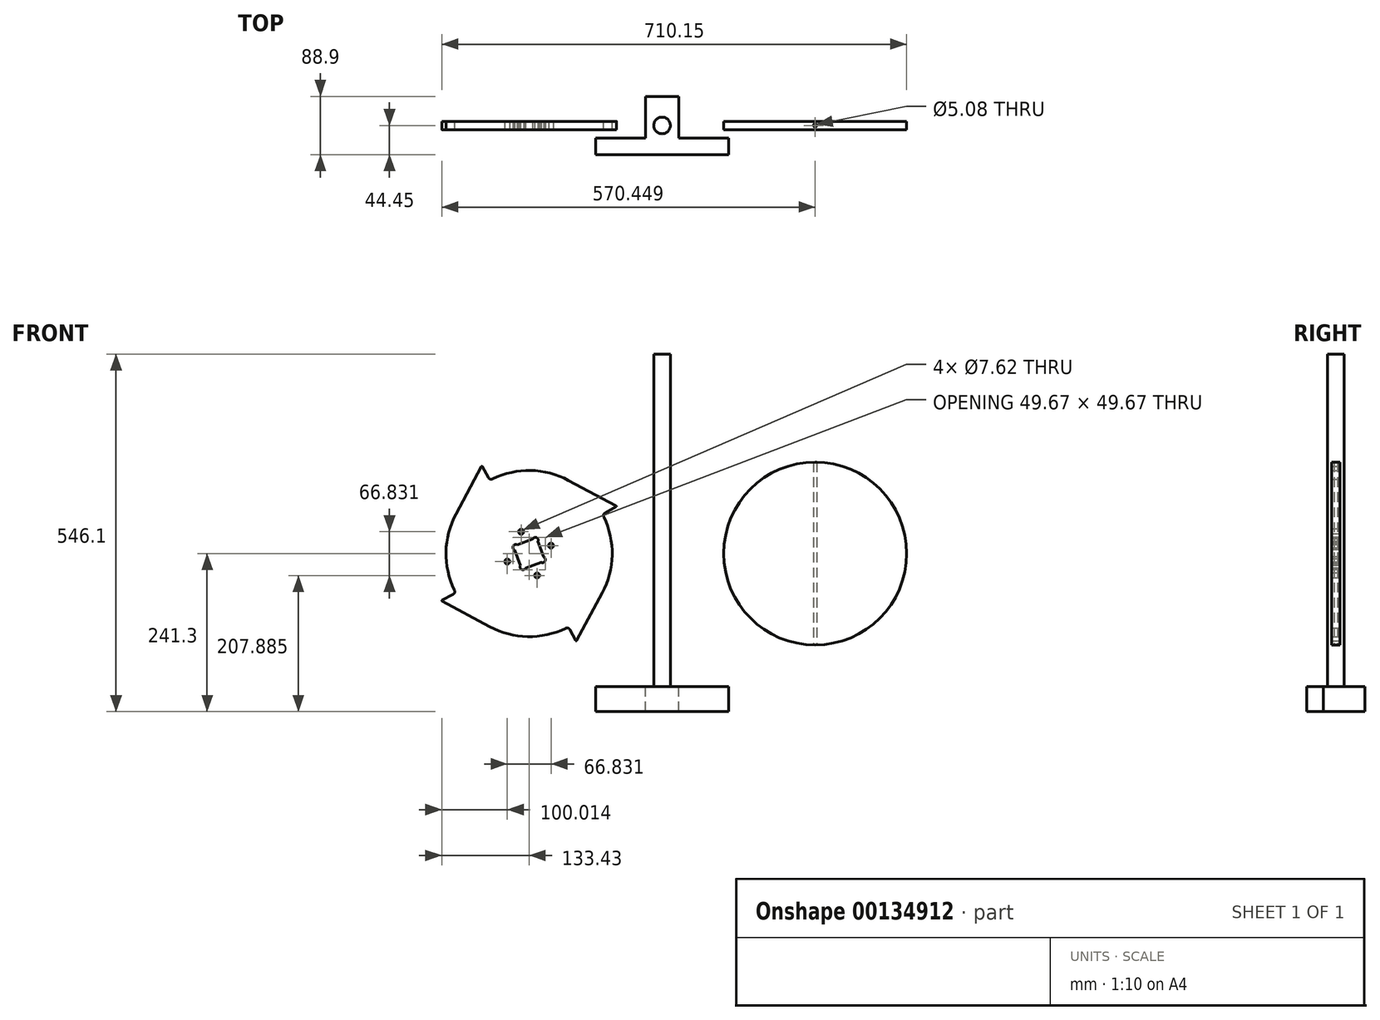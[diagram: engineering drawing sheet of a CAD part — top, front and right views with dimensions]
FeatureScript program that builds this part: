
annotation { "Feature Type Name" : "Feature", "Feature Type Description" : "" }
export const myFeature = defineFeature(function(context is Context, id is Id, definition is map)
    precondition{}
    {
        {
            var Q0;
            Q0=qCreatedBy(makeId("Front.planeOp"),FACE);
            var sketch = newSketch(context, id + "F0", { "sketchPlane" : qUnion([Q0])});
            skLineSegment(sketch, "E0", {"start": v(-203.2, 203.2) * mm, "end": v(-95.44, 310.96) * mm, "construction": true});
            skLineSegment(sketch, "E1", {"start": v(-203.2, 203.2) * mm, "end": v(-95.44, 95.44) * mm, "construction": true});
            skLineSegment(sketch, "E2", {"start": v(-203.2, 203.2) * mm, "end": v(-310.96, 95.44) * mm, "construction": true});
            skLineSegment(sketch, "E3", {"start": v(-203.2, 203.2) * mm, "end": v(-203.2, 409.98) * mm, "construction": true});
            skLineSegment(sketch, "E4", {"start": v(-91.3, 263.26) * mm, "end": v(-68.92, 275.27) * mm});
            skLineSegment(sketch, "E5", {"start": v(-143.14, 91.3) * mm, "end": v(-131.13, 68.92) * mm});
            skLineSegment(sketch, "E6", {"start": v(-315.1, 143.14) * mm, "end": v(-337.48, 131.13) * mm});
            skArc(sketch, "E7", {"start": v(-91.3, 263.26) * mm, "mid": v(-76.2, 203.2) * mm, "end": v(-91.3, 143.14) * mm});
            skArc(sketch, "E8", {"start": v(-143.14, 91.3) * mm, "mid": v(-203.2, 76.2) * mm, "end": v(-263.26, 91.3) * mm});
            skArc(sketch, "E9", {"start": v(-315.1, 143.14) * mm, "mid": v(-330.2, 203.2) * mm, "end": v(-315.1, 263.26) * mm});
            skLineSegment(sketch, "E10", {"start": v(-143.14, 315.1) * mm, "end": v(-68.92, 275.27) * mm});
            skLineSegment(sketch, "E11", {"start": v(-131.13, 68.92) * mm, "end": v(-91.3, 143.14) * mm});
            skLineSegment(sketch, "E12", {"start": v(-337.48, 131.13) * mm, "end": v(-263.26, 91.3) * mm});
            skLineSegment(sketch, "E13", {"start": v(-203.2, 203.2) * mm, "end": v(-293, 293) * mm, "construction": true});
            skArc(sketch, "E14.trimOffspring", {"start": v(-263.26, 315.1) * mm, "mid": v(-203.2, 330.2) * mm, "end": v(-143.14, 315.1) * mm});
            skLineSegment(sketch, "E15", {"start": v(-263.26, 315.1) * mm, "end": v(-275.27, 337.48) * mm});
            skLineSegment(sketch, "E16", {"start": v(-275.27, 337.48) * mm, "end": v(-315.1, 263.26) * mm});
            skSolve(sketch);
        }
        {
            var Q0;
            Q0=makeQuery(id+"F0.imprint","IMPRINT",FACE,{"disambiguationData":[TD([[makeQuery(id+"F0.imprint","IMPRINT",EDGE,{"derivedFrom":sQuery(id+"F0.wireOp",EDGE,"E4")}),1.0]])]});
            extrude(context, id + "F1", {"entities" : qUnion([Q0]), "endBound" : BoundingType.SYMMETRIC, "depth" : 12.7 * mm});
        }
        {
            var Q0;
            Q0=qCreatedBy(makeId("Front.planeOp"),FACE);
            var sketch = newSketch(context, id + "F2", { "sketchPlane" : qUnion([Q0])});
            skArc(sketch, "E17.0", {"start": v(-315.1, 143.14) * mm, "mid": v(-330.2, 203.2) * mm, "end": v(-315.1, 263.26) * mm, "construction": true});
            skLineSegment(sketch, "E18", {"start": v(-203.2, 203.2) * mm, "end": v(-57.25, 256.32) * mm, "construction": true});
            skLineSegment(sketch, "E19", {"start": v(-203.2, 203.2) * mm, "end": v(-203.2, 358.54) * mm, "construction": true});
            skLineSegment(sketch, "E20", {"start": v(-203.2, 203.2) * mm, "end": v(-359.68, 203.2) * mm, "construction": true});
            skPoint(sketch, "E20.endSnap0", {"position": v(-330.2, 203.2) * mm});
            skLineSegment(sketch, "E21", {"start": v(-203.2, 203.2) * mm, "end": v(-256.47, 349.55) * mm, "construction": true});
            skLineSegment(sketch, "E22", {"start": v(-227.62, 214.59) * mm, "end": v(-191.81, 227.62) * mm});
            skLineSegment(sketch, "E23", {"start": v(-191.81, 227.62) * mm, "end": v(-178.78, 191.81) * mm});
            skLineSegment(sketch, "E24", {"start": v(-178.78, 191.81) * mm, "end": v(-214.59, 178.78) * mm});
            skLineSegment(sketch, "E25", {"start": v(-227.62, 214.59) * mm, "end": v(-214.59, 178.78) * mm});
            skCircle(sketch, "E26", {"center": v(-169.78, 215.36) * mm, "radius": 3.81 * mm});
            skCircle(sketch, "E27", {"center": v(-215.36, 236.62) * mm, "radius": 3.81 * mm});
            skCircle(sketch, "E28.MirrorC", {"center": v(-236.62, 191.04) * mm, "radius": 3.81 * mm});
            skCircle(sketch, "E29.MirrorC", {"center": v(-191.04, 169.78) * mm, "radius": 3.81 * mm});
            skLineSegment(sketch, "E30", {"start": v(-203.2, 203.2) * mm, "end": v(-191.81, 227.62) * mm, "construction": true});
            skCircle(sketch, "E31", {"center": v(-193.71, 223.55) * mm, "radius": 4.5 * mm});
            skPoint(sketch, "E31.first.point", {"position": v(-189.64, 221.65) * mm});
            skPoint(sketch, "E31.second.point", {"position": v(-197.78, 225.44) * mm});
            skCircle(sketch, "E32.MirrorC", {"center": v(-182.85, 193.71) * mm, "radius": 4.5 * mm});
            skCircle(sketch, "E33.MirrorC", {"center": v(-223.55, 212.69) * mm, "radius": 4.5 * mm});
            skCircle(sketch, "E34.MirrorC", {"center": v(-212.69, 182.85) * mm, "radius": 4.5 * mm});
            skSolve(sketch);
        }
        {
            var Q0;
            Q0 = qSketchRegion(id + "F2", true);
            extrude(context, id + "F3", {"entities" : qUnion([Q0]), "operationType" : NewBodyOperationType.REMOVE, "endBound" : BoundingType.THROUGH_ALL, "oppositeDirection" : true, "depth" : 25.4 * mm, "hasSecondDirection" : true, "secondDirectionBound" : SecondDirectionBoundingType.THROUGH_ALL, "secondDirectionOppositeDirection" : false, "secondDirectionDepth" : 25.4 * mm});
        }
        {
            var Q0;
            Q0=makeQuery(id+"F1.opExtrude","SWEPT_EDGE",EDGE,{"disambiguationData":[OSD([sQuery(id+"F0.wireOp",EDGE,"E14.trimOffspring"),sQuery(id+"F0.wireOp",EDGE,"E15")])]});
            var Q1;
            Q1=makeQuery(id+"F1.opExtrude","SWEPT_EDGE",EDGE,{"disambiguationData":[OSD([sQuery(id+"F0.wireOp",EDGE,"E4"),sQuery(id+"F0.wireOp",EDGE,"E7")])]});
            var Q2;
            Q2=makeQuery(id+"F1.opExtrude","SWEPT_EDGE",EDGE,{"disambiguationData":[OSD([sQuery(id+"F0.wireOp",EDGE,"E5"),sQuery(id+"F0.wireOp",EDGE,"E8")])]});
            var Q3;
            Q3=makeQuery(id+"F1.opExtrude","SWEPT_EDGE",EDGE,{"disambiguationData":[OSD([sQuery(id+"F0.wireOp",EDGE,"E6"),sQuery(id+"F0.wireOp",EDGE,"E9")])]});
            fillet(context, id + "F4", {"entities" : qUnion([Q0, Q1, Q2, Q3]), "radius" : 5.08 * mm, "tangentPropagation" : true, "allowEdgeOverflow" : false});
        }
        {
            var Q0;
            Q0=makeQuery(id+"F1.opExtrude","SWEPT_EDGE",EDGE,{"disambiguationData":[OSD([sQuery(id+"F0.wireOp",EDGE,"E6"),sQuery(id+"F0.wireOp",EDGE,"E12")])]});
            var Q1;
            Q1=makeQuery(id+"F1.opExtrude","SWEPT_EDGE",EDGE,{"disambiguationData":[OSD([sQuery(id+"F0.wireOp",EDGE,"E5"),sQuery(id+"F0.wireOp",EDGE,"E11")])]});
            var Q2;
            Q2=makeQuery(id+"F1.opExtrude","SWEPT_EDGE",EDGE,{"disambiguationData":[OSD([sQuery(id+"F0.wireOp",EDGE,"E4"),sQuery(id+"F0.wireOp",EDGE,"E10")])]});
            var Q3;
            Q3=makeQuery(id+"F1.opExtrude","SWEPT_EDGE",EDGE,{"disambiguationData":[OSD([sQuery(id+"F0.wireOp",EDGE,"E15"),sQuery(id+"F0.wireOp",EDGE,"E16")])]});
            fillet(context, id + "F5", {"entities" : qUnion([Q0, Q1, Q2, Q3]), "radius" : 0.76 * mm, "tangentPropagation" : true, "allowEdgeOverflow" : false});
        }
        {
            var Q0;
            Q0=qCreatedBy(makeId("Front.planeOp"),FACE);
            var sketch = newSketch(context, id + "F6", { "sketchPlane" : qUnion([Q0])});
            skCircle(sketch, "E35", {"center": v(233.82, 203.2) * mm, "radius": 139.7 * mm});
            skArc(sketch, "E36.0", {"start": v(-298.26, 287.41) * mm, "mid": v(-99.01, 130.58) * mm, "end": v(-315.1, 263.26) * mm, "construction": true});
            skSolve(sketch);
        }
        {
            var Q0;
            Q0=makeQuery(id+"F6.imprint","IMPRINT",FACE,{"disambiguationData":[TD([[makeQuery(id+"F6.imprint","IMPRINT",EDGE,{"derivedFrom":sQuery(id+"F6.wireOp",EDGE,"E35")}),1.0]])]});
            extrude(context, id + "F7", {"entities" : qUnion([Q0]), "endBound" : BoundingType.SYMMETRIC, "depth" : 12.7 * mm});
        }
        {
            var Q0;
            Q0=qCreatedBy(makeId("Top.planeOp"),FACE);
            var sketch = newSketch(context, id + "F8", { "sketchPlane" : qUnion([Q0])});
            skCircle(sketch, "E37", {"center": v(0, 0) * mm, "radius": 12.7 * mm});
            skSolve(sketch);
        }
        {
            var Q0;
            Q0=makeQuery(id+"F8.imprint","IMPRINT",FACE,{"disambiguationData":[TD([[makeQuery(id+"F8.imprint","IMPRINT",EDGE,{"derivedFrom":sQuery(id+"F8.wireOp",EDGE,"E37")}),1.0]])]});
            extrude(context, id + "F9", {"entities" : qUnion([Q0]), "depth" : 508 * mm});
        }
        {
            var Q0;
            Q0=qCreatedBy(makeId("Right.planeOp"),FACE);
            var sketch = newSketch(context, id + "F10", { "sketchPlane" : qUnion([Q0])});
            skLineSegment(sketch, "E38", {"start": v(0, 0) * mm, "end": v(0, -51.2) * mm, "construction": true});
            skLineSegment(sketch, "E39.bottom", {"start": v(-44.45, 0) * mm, "end": v(44.45, 0) * mm});
            skLineSegment(sketch, "E39.top", {"start": v(-44.45, -38.1) * mm, "end": v(44.45, -38.1) * mm});
            skLineSegment(sketch, "E39.left", {"start": v(-44.45, 0) * mm, "end": v(-44.45, -38.1) * mm});
            skLineSegment(sketch, "E39.right", {"start": v(44.45, 0) * mm, "end": v(44.45, -38.1) * mm});
            skSolve(sketch);
        }
        {
            var Q0;
            Q0=makeQuery(id+"F10.imprint","IMPRINT",FACE,{"disambiguationData":[TD([[makeQuery(id+"F10.imprint","IMPRINT",EDGE,{"derivedFrom":sQuery(id+"F10.wireOp",EDGE,"E39.bottom")}),-1.0]])]});
            extrude(context, id + "F11", {"entities" : qUnion([Q0]), "operationType" : NewBodyOperationType.ADD, "endBound" : BoundingType.SYMMETRIC, "depth" : 203.2 * mm});
        }
        {
            var Q0;
            Q0=qCreatedBy(makeId("Top.planeOp"),FACE);
            var sketch = newSketch(context, id + "F12", { "sketchPlane" : qUnion([Q0])});
            skLineSegment(sketch, "E40.0", {"start": v(373.52, 6.35) * mm, "end": v(94.12, 6.35) * mm, "construction": true});
            skLineSegment(sketch, "E41.0", {"start": v(373.52, -6.35) * mm, "end": v(94.12, -6.35) * mm, "construction": true});
            skLineSegment(sketch, "E42", {"start": v(233.82, 6.35) * mm, "end": v(233.82, -6.35) * mm, "construction": true});
            skCircle(sketch, "E43", {"center": v(233.82, 0) * mm, "radius": 2.54 * mm});
            skSolve(sketch);
        }
        {
            var Q0;
            Q0=makeQuery(id+"F12.imprint","IMPRINT",FACE,{"disambiguationData":[TD([[makeQuery(id+"F12.imprint","IMPRINT",EDGE,{"derivedFrom":sQuery(id+"F12.wireOp",EDGE,"E43")}),1.0]])]});
            extrude(context, id + "F13", {"entities" : qUnion([Q0]), "operationType" : NewBodyOperationType.REMOVE, "endBound" : BoundingType.THROUGH_ALL, "depth" : 25.4 * mm});
        }
        {
            var Q0;
            Q0=makeQuery(id+"F11.opExtrude","SWEPT_FACE",FACE,{"disambiguationData":[OSD([sQuery(id+"F10.wireOp",EDGE,"E39.bottom")])]});
            var sketch = newSketch(context, id + "F14", { "sketchPlane" : qUnion([Q0])});
            skLineSegment(sketch, "E44", {"start": v(0, 0) * mm, "end": v(0, 63.61) * mm, "construction": true});
            skLineSegment(sketch, "E45.bottom", {"start": v(101.6, 44.45) * mm, "end": v(25.4, 44.45) * mm});
            skLineSegment(sketch, "E45.top", {"start": v(101.6, -19.05) * mm, "end": v(25.4, -19.05) * mm});
            skLineSegment(sketch, "E45.left", {"start": v(101.6, 44.45) * mm, "end": v(101.6, -19.05) * mm});
            skLineSegment(sketch, "E45.right", {"start": v(25.4, 44.45) * mm, "end": v(25.4, -19.05) * mm});
            skLineSegment(sketch, "E46.MirrorCS", {"start": v(-25.4, 44.45) * mm, "end": v(-25.4, -19.05) * mm});
            skLineSegment(sketch, "E47.MirrorCS", {"start": v(-101.6, 44.45) * mm, "end": v(-101.6, -19.05) * mm});
            skLineSegment(sketch, "E48.MirrorCS", {"start": v(-101.6, 44.45) * mm, "end": v(-25.4, 44.45) * mm});
            skLineSegment(sketch, "E49.MirrorCS", {"start": v(-101.6, -19.05) * mm, "end": v(-25.4, -19.05) * mm});
            skSolve(sketch);
        }
        {
            var Q0;
            Q0=makeQuery(id+"F14.imprint","IMPRINT",FACE,{"disambiguationData":[TD([[makeQuery(id+"F14.imprint","IMPRINT",EDGE,{"derivedFrom":sQuery(id+"F14.wireOp",EDGE,"E46.MirrorCS")}),-1.0]])]});
            var Q1;
            Q1=makeQuery(id+"F14.imprint","IMPRINT",FACE,{"disambiguationData":[TD([[makeQuery(id+"F14.imprint","IMPRINT",EDGE,{"derivedFrom":sQuery(id+"F14.wireOp",EDGE,"E45.bottom")}),1.0]])]});
            extrude(context, id + "F15", {"entities" : qUnion([Q0, Q1]), "operationType" : NewBodyOperationType.REMOVE, "endBound" : BoundingType.THROUGH_ALL, "oppositeDirection" : true, "depth" : 25.4 * mm});
        }
    });
